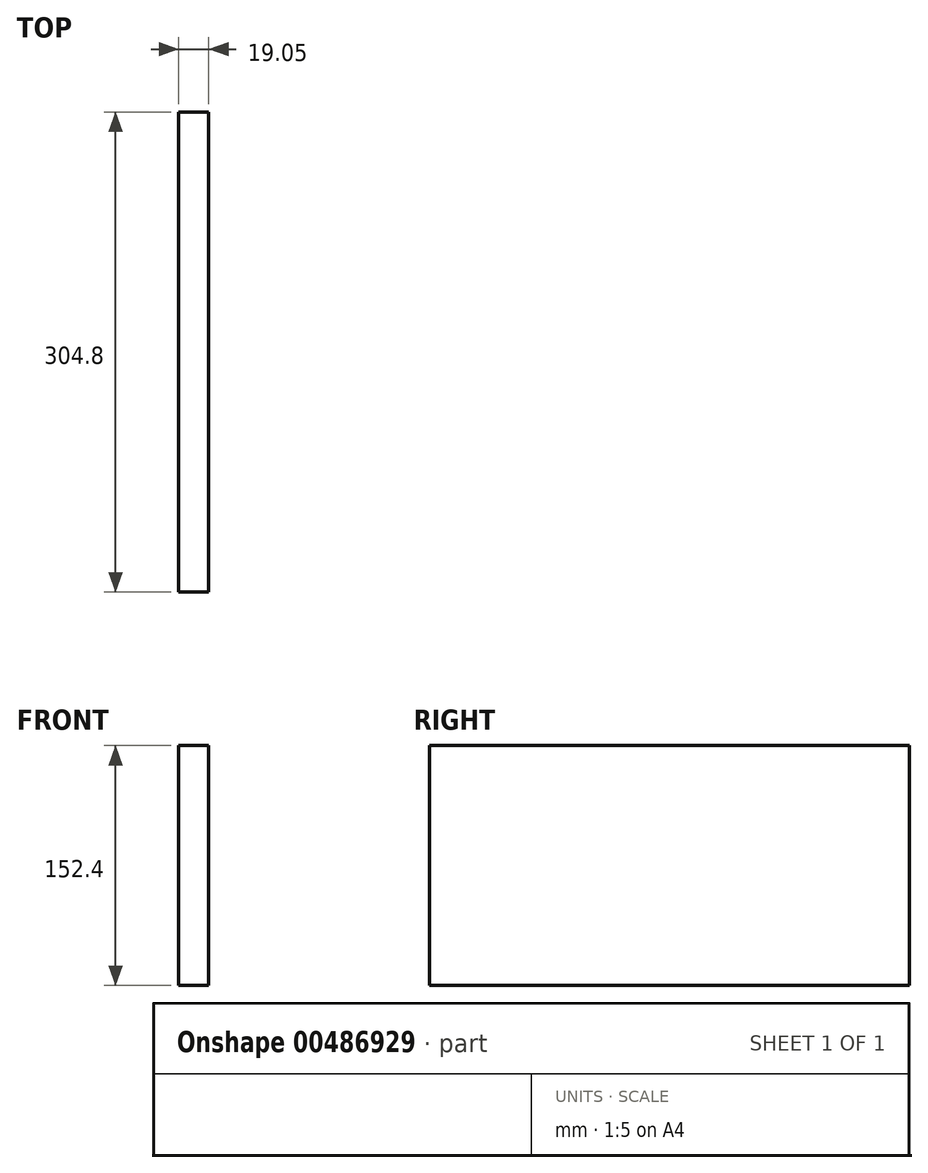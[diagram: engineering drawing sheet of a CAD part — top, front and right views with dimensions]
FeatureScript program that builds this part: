
annotation { "Feature Type Name" : "Feature", "Feature Type Description" : "" }
export const myFeature = defineFeature(function(context is Context, id is Id, definition is map)
    precondition{}
    {
        {
            var Q0;
            Q0=qCreatedBy(makeId("Right.planeOp"),FACE);
            var sketch = newSketch(context, id + "F0", { "sketchPlane" : qUnion([Q0])});
            skLineSegment(sketch, "E0.bottom", {"start": v(-152.4, 76.2) * mm, "end": v(152.4, 76.2) * mm});
            skLineSegment(sketch, "E0.top", {"start": v(-152.4, -76.2) * mm, "end": v(152.4, -76.2) * mm});
            skLineSegment(sketch, "E0.left", {"start": v(-152.4, 76.2) * mm, "end": v(-152.4, -76.2) * mm});
            skLineSegment(sketch, "E0.right", {"start": v(152.4, 76.2) * mm, "end": v(152.4, -76.2) * mm});
            skSolve(sketch);
        }
        {
            var Q0;
            Q0=makeQuery(id+"F0.imprint","IMPRINT",FACE,{"disambiguationData":[TD([[makeQuery(id+"F0.imprint","IMPRINT",EDGE,{"derivedFrom":sQuery(id+"F0.wireOp",EDGE,"E0.bottom")}),-1.0]])]});
            var Q1;
            Q1=sQuery(id+"F0.wireOp",EDGE,"E0.left");
            var Q2;
            Q2=sQuery(id+"F0.wireOp",EDGE,"E0.bottom");
            var Q3;
            Q3=sQuery(id+"F0.wireOp",EDGE,"E0.top");
            var Q4;
            Q4=sQuery(id+"F0.wireOp",EDGE,"E0.right");
            extrude(context, id + "F1", {"entities" : qUnion([Q0]), "surfaceEntities" : qUnion([Q1, Q2, Q3, Q4]), "oppositeDirection" : true, "depth" : 19.05 * mm});
        }
    });
